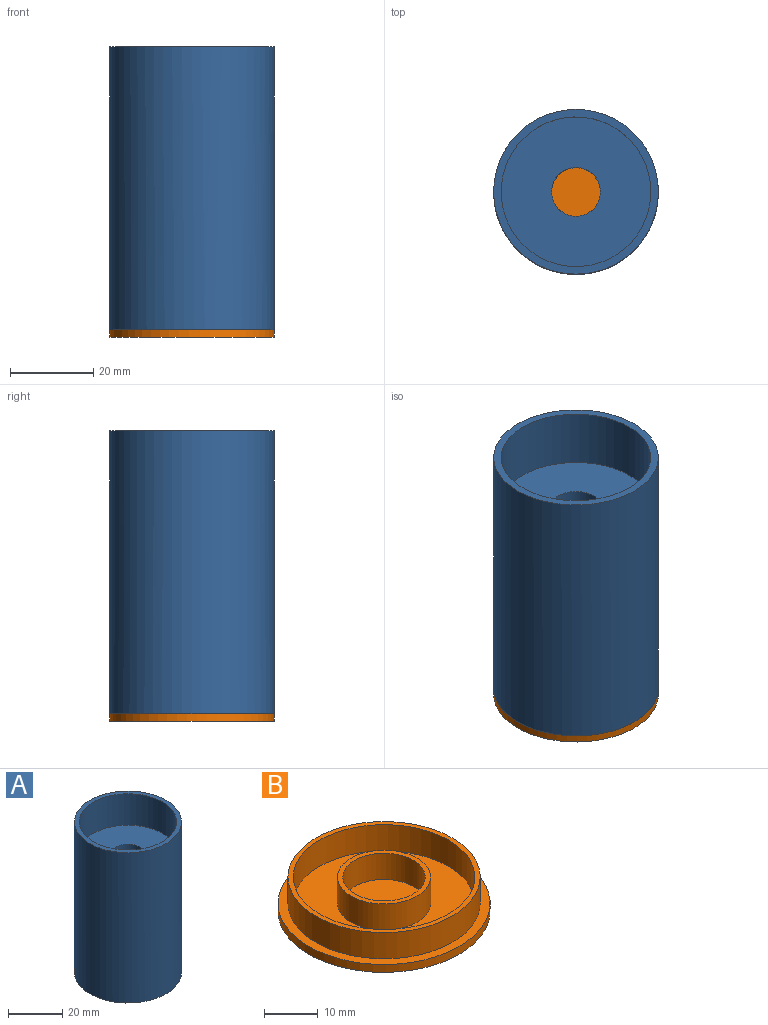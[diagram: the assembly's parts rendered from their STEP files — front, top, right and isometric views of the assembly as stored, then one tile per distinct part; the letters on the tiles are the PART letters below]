
ASSEMBLY  parts=2 mates=1
PART A: 10 faces, bbox 39.6x39.6x68 mm
  f0: plane 36x36mm, normal (0,0,-1), area 832.8mm2, adj f6,f8
  f1: cylinder r=18mm len=36mm, axis (0,0,-1), area 1606mm2, adj f3,f4
  f2: cylinder r=19.8mm len=68mm, axis (0,0,-1), area 8459.7mm2, adj f3,f9
  f3: plane 39.6x39.6mm, normal (0,0,1), area 213.8mm2, adj f1,f2
  f4: plane 36x36mm, normal (0,0,1), area 909.4mm2, adj f1,f5
  f5: cylinder r=5.88mm len=53.8mm, axis (0,0,-1), area 1986mm2, adj f4,f7
  f6: cylinder r=7.68mm len=52mm, axis (0,0,1), area 2507.6mm2, adj f0,f7
  f7: plane 15.35x15.35mm, normal (0,0,-1), area 76.6mm2, adj f5,f6
  f8: cylinder r=18mm len=52mm, axis (0,0,1), area 5881.1mm2, adj f0,f9
  f9: plane 39.6x39.6mm, normal (0,0,-1), area 213.8mm2, adj f2,f8
PART B: 11 faces, bbox 39.6x39.6x7.8 mm
  f0: cylinder r=16.95mm len=33.9mm, axis (0,0,-1), area 639mm2, adj f2,f6
  f1: cylinder r=17.95mm len=35.9mm, axis (0,0,-1), area 676.7mm2, adj f2,f5
  f2: plane 35.9x35.9mm, normal (0,0,1), area 109.6mm2, adj f0,f1
  f3: plane 39.6x39.6mm, normal (0,0,-1), area 1231.6mm2, adj f4
  f4: cylinder r=19.8mm len=39.6mm, axis (0,0,1), area 223.9mm2, adj f3,f5
  f5: plane 39.6x39.6mm, normal (0,0,1), area 219.4mm2, adj f1,f4
  f6: plane 33.9x33.9mm, normal (0,0,1), area 664.8mm2, adj f0,f8
  f7: cylinder r=7.7mm len=15.4mm, axis (0,0,-1), area 290.3mm2, adj f9,f10
  f8: cylinder r=8.7mm len=17.4mm, axis (0,0,-1), area 328mm2, adj f6,f9
  f9: plane 17.4x17.4mm, normal (0,0,1), area 51.5mm2, adj f7,f8
  f10: plane 15.4x15.4mm, normal (0,0,1), area 186.3mm2, adj f7
PLACE A t=(-13.51,-13.09,11.86)mm
PLACE B t=(-13.51,-13.09,-41.94)mm
MATE fastened B.f7 <-> A.f5  axis (0,0,1) through (-13.51,-13.09,-41.94)mm
